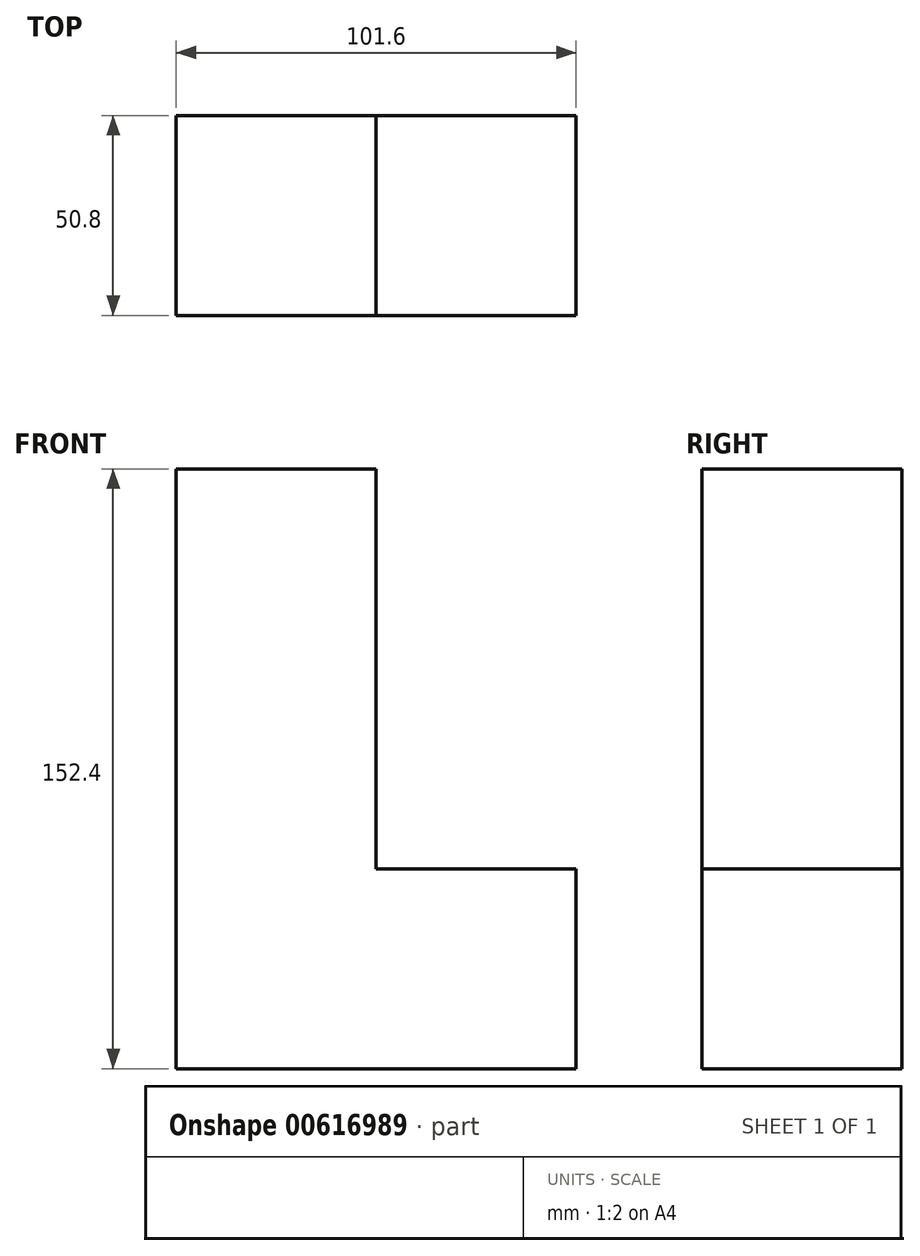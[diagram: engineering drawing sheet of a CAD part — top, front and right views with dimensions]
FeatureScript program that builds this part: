
annotation { "Feature Type Name" : "Feature", "Feature Type Description" : "" }
export const myFeature = defineFeature(function(context is Context, id is Id, definition is map)
    precondition{}
    {
        {
            var Q0;
            Q0=qCreatedBy(makeId("Front.planeOp"),FACE);
            var sketch = newSketch(context, id + "F0", { "sketchPlane" : qUnion([Q0])});
            skLineSegment(sketch, "E0.bottom", {"start": v(-44.9, -39.84) * mm, "end": v(5.9, -39.84) * mm});
            skLineSegment(sketch, "E0.top", {"start": v(-44.9, 112.56) * mm, "end": v(5.9, 112.56) * mm});
            skLineSegment(sketch, "E0.left", {"start": v(-44.9, -39.84) * mm, "end": v(-44.9, 112.56) * mm});
            skLineSegment(sketch, "E0.right", {"start": v(5.9, -39.84) * mm, "end": v(5.9, 112.56) * mm});
            skPoint(sketch, "E0.middle", {"position": v(-19.5, 36.36) * mm});
            skLineSegment(sketch, "E1.bottom", {"start": v(5.9, -39.84) * mm, "end": v(56.7, -39.84) * mm});
            skLineSegment(sketch, "E1.top", {"start": v(5.9, 10.96) * mm, "end": v(56.7, 10.96) * mm});
            skLineSegment(sketch, "E1.left", {"start": v(5.9, -39.84) * mm, "end": v(5.9, 10.96) * mm});
            skLineSegment(sketch, "E1.right", {"start": v(56.7, -39.84) * mm, "end": v(56.7, 10.96) * mm});
            skPoint(sketch, "E1.middle", {"position": v(31.3, -14.44) * mm});
            skSolve(sketch);
        }
        {
            var Q0;
            Q0 = qSketchRegion(id + "F0", true);
            extrude(context, id + "F1", {"entities" : qUnion([Q0]), "endBound" : BoundingType.SYMMETRIC, "depth" : 50.8 * mm, "offsetDistance" : 25.4 * mm});
        }
    });
